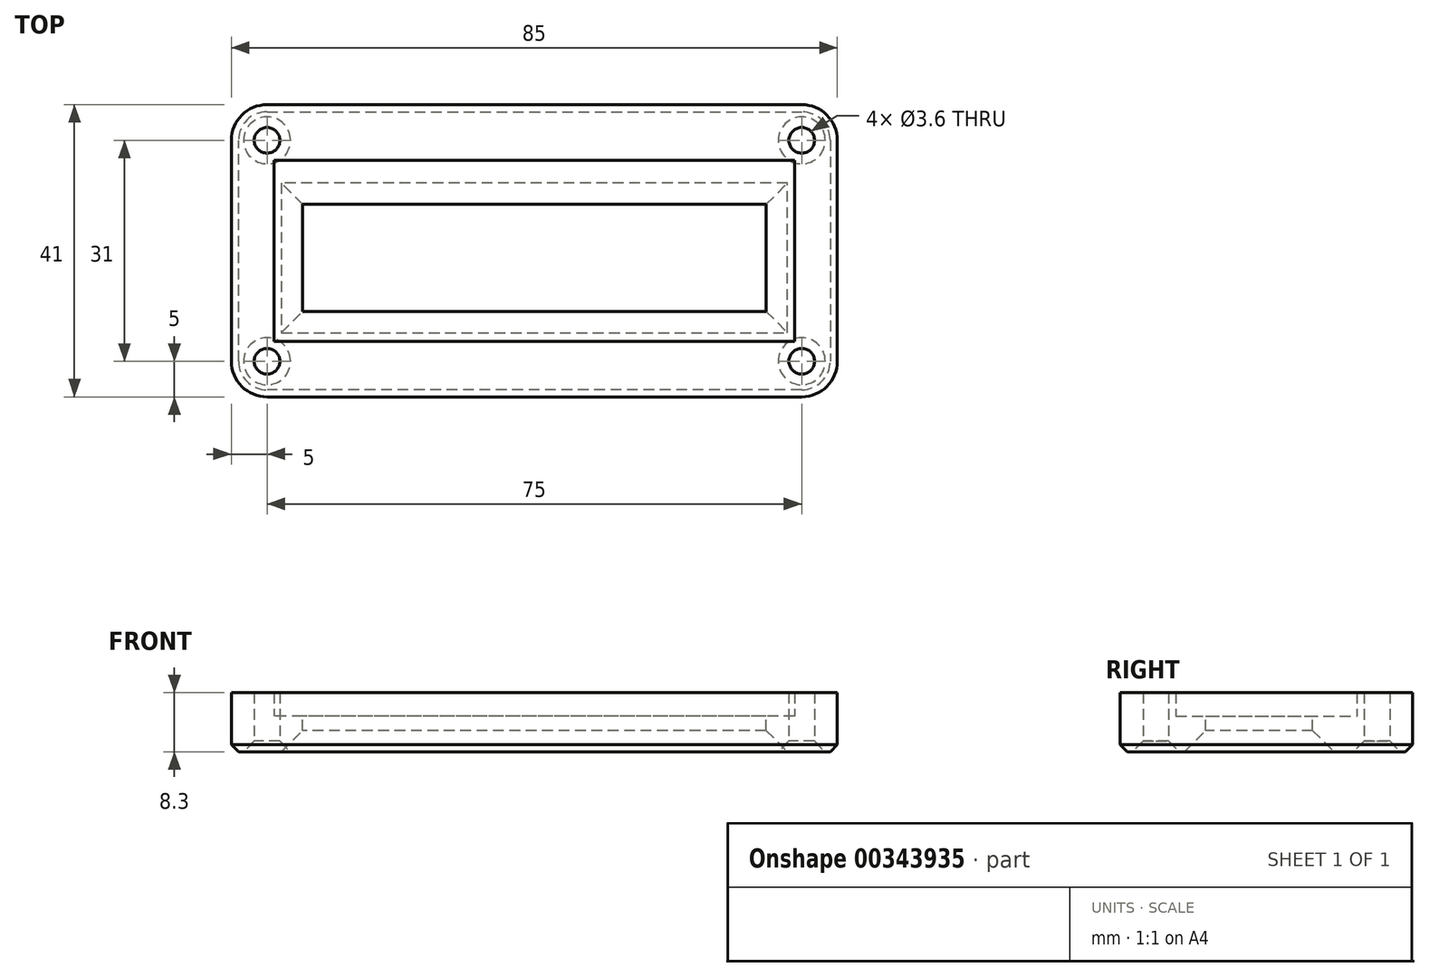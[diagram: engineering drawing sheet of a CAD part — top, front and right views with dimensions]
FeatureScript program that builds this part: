
annotation { "Feature Type Name" : "Feature", "Feature Type Description" : "" }
export const myFeature = defineFeature(function(context is Context, id is Id, definition is map)
    precondition{}
    {
        {
            var Q0;
            Q0=qCreatedBy(makeId("Top.planeOp"),FACE);
            var sketch = newSketch(context, id + "F0", { "sketchPlane" : qUnion([Q0])});
            skPoint(sketch, "E0.middle", {"position": v(0, 0) * mm});
            skCircle(sketch, "E1", {"center": v(-37.5, 15.5) * mm, "radius": 1.8 * mm});
            skCircle(sketch, "E2", {"center": v(37.5, 15.5) * mm, "radius": 1.8 * mm});
            skCircle(sketch, "E3", {"center": v(37.5, -15.5) * mm, "radius": 1.8 * mm});
            skCircle(sketch, "E4", {"center": v(-37.5, -15.5) * mm, "radius": 1.8 * mm});
            skLineSegment(sketch, "E5", {"start": v(0, 0) * mm, "end": v(0, -1) * mm});
            skLineSegment(sketch, "E6.bottom", {"start": v(32.5, -8.5) * mm, "end": v(-32.5, -8.5) * mm});
            skLineSegment(sketch, "E6.top", {"start": v(32.5, 6.5) * mm, "end": v(-32.5, 6.5) * mm});
            skLineSegment(sketch, "E6.left", {"start": v(32.5, -8.5) * mm, "end": v(32.5, 6.5) * mm});
            skLineSegment(sketch, "E6.right", {"start": v(-32.5, -8.5) * mm, "end": v(-32.5, 6.5) * mm});
            skPoint(sketch, "E6.middle", {"position": v(0, -1) * mm});
            skLineSegment(sketch, "E7.bottom", {"start": v(35.5, -13) * mm, "end": v(-35.5, -13) * mm, "construction": true});
            skLineSegment(sketch, "E7.top", {"start": v(35.5, 11) * mm, "end": v(-35.5, 11) * mm, "construction": true});
            skLineSegment(sketch, "E7.left", {"start": v(35.5, -13) * mm, "end": v(35.5, 11) * mm, "construction": true});
            skLineSegment(sketch, "E7.right", {"start": v(-35.5, -13) * mm, "end": v(-35.5, 11) * mm, "construction": true});
            skLineSegment(sketch, "E8.bottom", {"start": v(36.5, -12.7) * mm, "end": v(-36.5, -12.7) * mm});
            skLineSegment(sketch, "E8.top", {"start": v(36.5, 12.7) * mm, "end": v(-36.5, 12.7) * mm});
            skLineSegment(sketch, "E8.left", {"start": v(36.5, -12.7) * mm, "end": v(36.5, 12.7) * mm});
            skLineSegment(sketch, "E8.right", {"start": v(-36.5, -12.7) * mm, "end": v(-36.5, 12.7) * mm});
            skLineSegment(sketch, "E9.bottom", {"start": v(42.5, -20.5) * mm, "end": v(-42.5, -20.5) * mm});
            skLineSegment(sketch, "E9.top", {"start": v(42.5, 20.5) * mm, "end": v(-42.5, 20.5) * mm});
            skLineSegment(sketch, "E9.left", {"start": v(42.5, -20.5) * mm, "end": v(42.5, 20.5) * mm});
            skLineSegment(sketch, "E9.right", {"start": v(-42.5, -20.5) * mm, "end": v(-42.5, 20.5) * mm});
            skCircle(sketch, "E10", {"center": v(-37.5, 15.5) * mm, "radius": 3.25 * mm, "construction": true});
            skCircle(sketch, "E11", {"center": v(37.5, 15.5) * mm, "radius": 3.25 * mm, "construction": true});
            skCircle(sketch, "E12", {"center": v(37.5, -15.5) * mm, "radius": 3.25 * mm, "construction": true});
            skCircle(sketch, "E13", {"center": v(-37.5, -15.5) * mm, "radius": 3.25 * mm, "construction": true});
            skSolve(sketch);
        }
        {
            var Q0;
            Q0=makeQuery(id+"F0.imprint","IMPRINT",FACE,{"disambiguationData":[TD([[makeQuery(id+"F0.imprint","IMPRINT",EDGE,{"derivedFrom":sQuery(id+"F0.wireOp",EDGE,"E1")}),-1.0]])]});
            extrude(context, id + "F1", {"entities" : qUnion([Q0]), "depth" : 3.3 * mm});
        }
        {
            var Q0;
            Q0=makeQuery(id+"F0.imprint","IMPRINT",FACE,{"disambiguationData":[TD([[makeQuery(id+"F0.imprint","IMPRINT",EDGE,{"derivedFrom":sQuery(id+"F0.wireOp",EDGE,"E6.bottom")}),1.0]])]});
            var Q1;
            Q1=makeQuery(id+"F0.imprint","IMPRINT",FACE,{"disambiguationData":[TD([[makeQuery(id+"F0.imprint","IMPRINT",EDGE,{"derivedFrom":sQuery(id+"F0.wireOp",EDGE,"E1")}),-1.0]])]});
            extrude(context, id + "F2", {"entities" : qUnion([Q0, Q1]), "operationType" : NewBodyOperationType.ADD, "depth" : -5 * mm});
        }
        {
            var Q0;
            {var subQ0=sQuery(id+"F0.wireOp",EDGE,"E9.right");var subQ1=sQuery(id+"F0.wireOp",EDGE,"E9.top");Q0=makeQuery(id+"F2.boolean.opBoolean","MERGE",EDGE,{"derivedFrom":[makeQuery(id+"F1.opExtrude","SWEPT_EDGE",EDGE,{"disambiguationData":[OSD([subQ1,subQ0])]}),makeQuery(id+"F2.opExtrude","SWEPT_EDGE",EDGE,{"disambiguationData":[OSD([subQ1,subQ0])]})]});}
            var Q1;
            {var subQ0=sQuery(id+"F0.wireOp",EDGE,"E9.right");var subQ1=sQuery(id+"F0.wireOp",EDGE,"E9.bottom");Q1=makeQuery(id+"F2.boolean.opBoolean","MERGE",EDGE,{"derivedFrom":[makeQuery(id+"F1.opExtrude","SWEPT_EDGE",EDGE,{"disambiguationData":[OSD([subQ1,subQ0])]}),makeQuery(id+"F2.opExtrude","SWEPT_EDGE",EDGE,{"disambiguationData":[OSD([subQ1,subQ0])]})]});}
            var Q2;
            {var subQ0=sQuery(id+"F0.wireOp",EDGE,"E9.left");var subQ1=sQuery(id+"F0.wireOp",EDGE,"E9.top");Q2=makeQuery(id+"F2.boolean.opBoolean","MERGE",EDGE,{"derivedFrom":[makeQuery(id+"F1.opExtrude","SWEPT_EDGE",EDGE,{"disambiguationData":[OSD([subQ1,subQ0])]}),makeQuery(id+"F2.opExtrude","SWEPT_EDGE",EDGE,{"disambiguationData":[OSD([subQ1,subQ0])]})]});}
            var Q3;
            {var subQ0=sQuery(id+"F0.wireOp",EDGE,"E9.left");var subQ1=sQuery(id+"F0.wireOp",EDGE,"E9.bottom");Q3=makeQuery(id+"F2.boolean.opBoolean","MERGE",EDGE,{"derivedFrom":[makeQuery(id+"F1.opExtrude","SWEPT_EDGE",EDGE,{"disambiguationData":[OSD([subQ1,subQ0])]}),makeQuery(id+"F2.opExtrude","SWEPT_EDGE",EDGE,{"disambiguationData":[OSD([subQ1,subQ0])]})]});}
            fillet(context, id + "F3", {"entities" : qUnion([Q0, Q1, Q2, Q3]), "radius" : 5 * mm, "tangentPropagation" : true, "allowEdgeOverflow" : false});
        }
        {
            var Q0;
            Q0=makeQuery(id+"F2.opExtrude","CAP_EDGE",EDGE,{"disambiguationData":[OSD([sQuery(id+"F0.wireOp",EDGE,"E6.bottom")])],"isStart":false});
            var Q1;
            Q1=makeQuery(id+"F2.opExtrude","CAP_EDGE",EDGE,{"disambiguationData":[OSD([sQuery(id+"F0.wireOp",EDGE,"E6.right")])],"isStart":false});
            var Q2;
            Q2=makeQuery(id+"F2.opExtrude","CAP_EDGE",EDGE,{"disambiguationData":[OSD([sQuery(id+"F0.wireOp",EDGE,"E6.top")])],"isStart":false});
            var Q3;
            Q3=makeQuery(id+"F2.opExtrude","CAP_EDGE",EDGE,{"disambiguationData":[OSD([sQuery(id+"F0.wireOp",EDGE,"E6.left")])],"isStart":false});
            chamfer(context, id + "F4", {"entities" : qUnion([Q0, Q1, Q2, Q3]), "width" : 3 * mm, "tangentPropagation" : true});
        }
        {
            var Q0;
            Q0=makeQuery(id+"F2.opExtrude","CAP_EDGE",EDGE,{"disambiguationData":[OSD([sQuery(id+"F0.wireOp",EDGE,"E9.right")])],"isStart":false});
            chamfer(context, id + "F5", {"entities" : qUnion([Q0]), "width" : 1 * mm, "tangentPropagation" : true});
        }
        {
            var Q0;
            Q0=makeQuery(id+"F2.opExtrude","CAP_EDGE",EDGE,{"disambiguationData":[OSD([sQuery(id+"F0.wireOp",EDGE,"E1")])],"isStart":false});
            var Q1;
            Q1=makeQuery(id+"F2.opExtrude","CAP_EDGE",EDGE,{"disambiguationData":[OSD([sQuery(id+"F0.wireOp",EDGE,"E4")])],"isStart":false});
            var Q2;
            Q2=makeQuery(id+"F2.opExtrude","CAP_EDGE",EDGE,{"disambiguationData":[OSD([sQuery(id+"F0.wireOp",EDGE,"E3")])],"isStart":false});
            var Q3;
            Q3=makeQuery(id+"F2.opExtrude","CAP_EDGE",EDGE,{"disambiguationData":[OSD([sQuery(id+"F0.wireOp",EDGE,"E2")])],"isStart":false});
            chamfer(context, id + "F6", {"entities" : qUnion([Q0, Q1, Q2, Q3]), "width" : 1.5 * mm, "tangentPropagation" : true});
        }
    });
